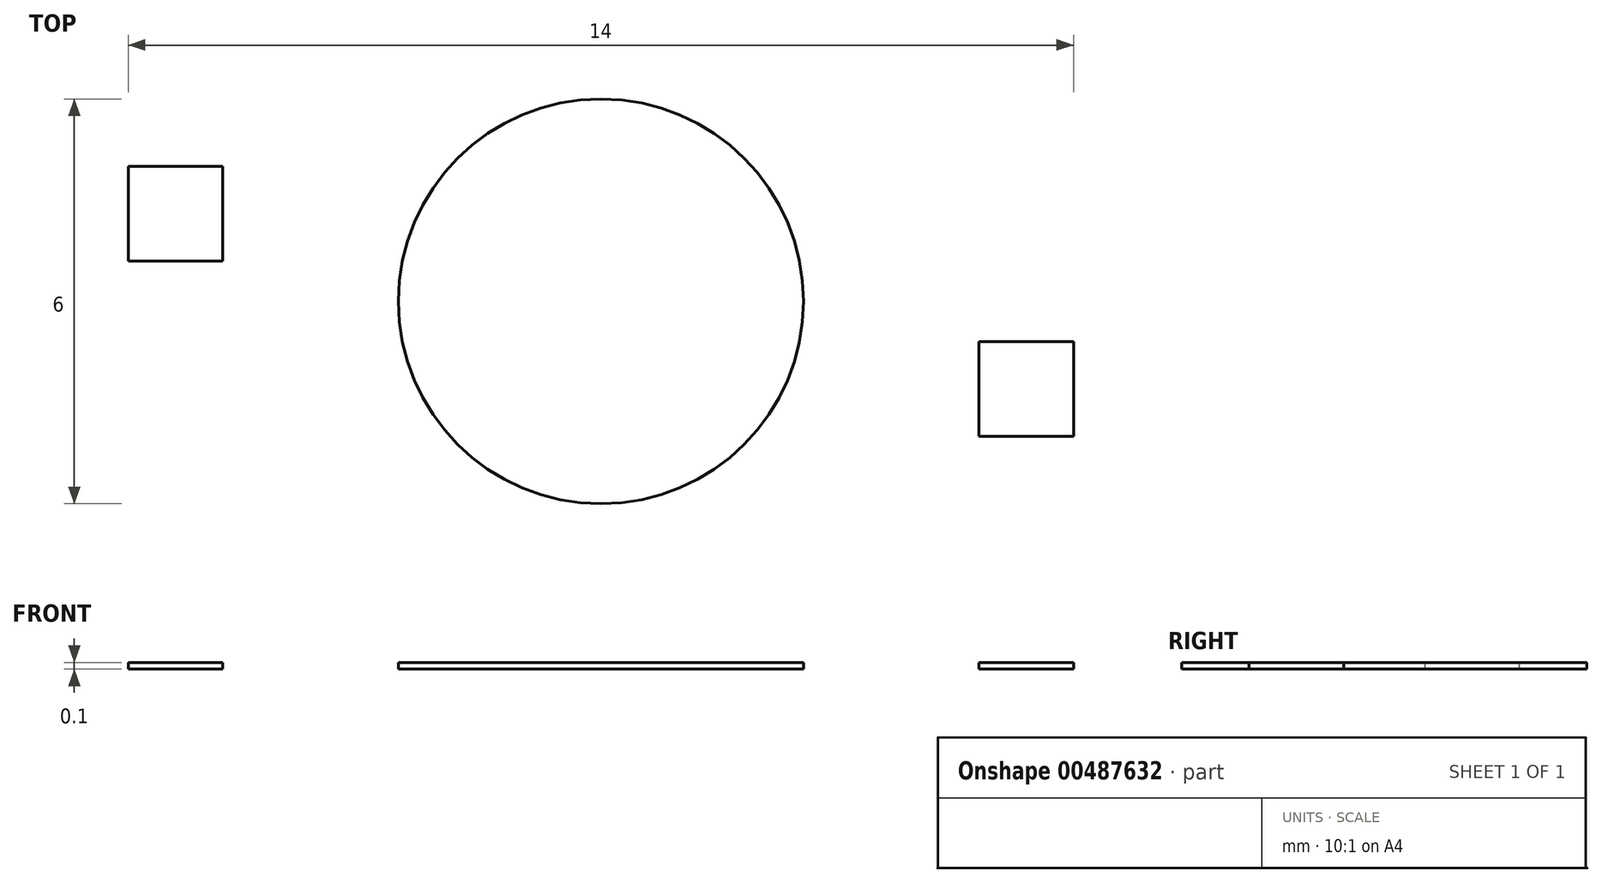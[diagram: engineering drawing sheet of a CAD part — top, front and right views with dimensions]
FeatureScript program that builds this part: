
annotation { "Feature Type Name" : "Feature", "Feature Type Description" : "" }
export const myFeature = defineFeature(function(context is Context, id is Id, definition is map)
    precondition{}
    {
        {
            var Q0;
            Q0=qCreatedBy(makeId("Top.planeOp"),FACE);
            var sketch = newSketch(context, id + "F0", { "sketchPlane" : qUnion([Q0])});
            skCircle(sketch, "E0", {"center": v(0, 0) * mm, "radius": 3 * mm});
            skLineSegment(sketch, "E1.bottom", {"start": v(-7, 2) * mm, "end": v(-5.6, 2) * mm});
            skLineSegment(sketch, "E1.top", {"start": v(-7, 0.6) * mm, "end": v(-5.6, 0.6) * mm});
            skLineSegment(sketch, "E1.left", {"start": v(-7, 2) * mm, "end": v(-7, 0.6) * mm});
            skLineSegment(sketch, "E1.right", {"start": v(-5.6, 2) * mm, "end": v(-5.6, 0.6) * mm});
            skLineSegment(sketch, "E2.bottom", {"start": v(5.6, -0.6) * mm, "end": v(7, -0.6) * mm});
            skLineSegment(sketch, "E2.top", {"start": v(5.6, -2) * mm, "end": v(7, -2) * mm});
            skLineSegment(sketch, "E2.left", {"start": v(5.6, -0.6) * mm, "end": v(5.6, -2) * mm});
            skLineSegment(sketch, "E2.right", {"start": v(7, -0.6) * mm, "end": v(7, -2) * mm});
            skLineSegment(sketch, "E3", {"start": v(-5.6, 0.6) * mm, "end": v(-5.6, 0) * mm, "construction": true});
            skLineSegment(sketch, "E4", {"start": v(5.6, -0.6) * mm, "end": v(5.6, 0) * mm, "construction": true});
            skLineSegment(sketch, "E5", {"start": v(5.6, -2) * mm, "end": v(0, -2) * mm, "construction": true});
            skLineSegment(sketch, "E6", {"start": v(-5.6, 2) * mm, "end": v(0, 2) * mm, "construction": true});
            skCircle(sketch, "E7", {"center": v(0, 0) * mm, "radius": 10 * mm});
            skCircle(sketch, "E8", {"center": v(0, 0) * mm, "radius": 8.8 * mm});
            skSolve(sketch);
        }
        {
            var Q0;
            Q0=makeQuery(id+"F0.imprint","IMPRINT",FACE,{"disambiguationData":[TD([[makeQuery(id+"F0.imprint","IMPRINT",EDGE,{"derivedFrom":sQuery(id+"F0.wireOp",EDGE,"E0")}),1.0]])]});
            var Q1;
            Q1=makeQuery(id+"F0.imprint","IMPRINT",FACE,{"disambiguationData":[TD([[makeQuery(id+"F0.imprint","IMPRINT",EDGE,{"derivedFrom":sQuery(id+"F0.wireOp",EDGE,"E2.bottom")}),-1.0]])]});
            var Q2;
            Q2=makeQuery(id+"F0.imprint","IMPRINT",FACE,{"disambiguationData":[TD([[makeQuery(id+"F0.imprint","IMPRINT",EDGE,{"derivedFrom":sQuery(id+"F0.wireOp",EDGE,"E1.bottom")}),-1.0]])]});
            extrude(context, id + "F1", {"entities" : qUnion([Q0, Q1, Q2]), "depth" : 0.1 * mm});
        }
    });
